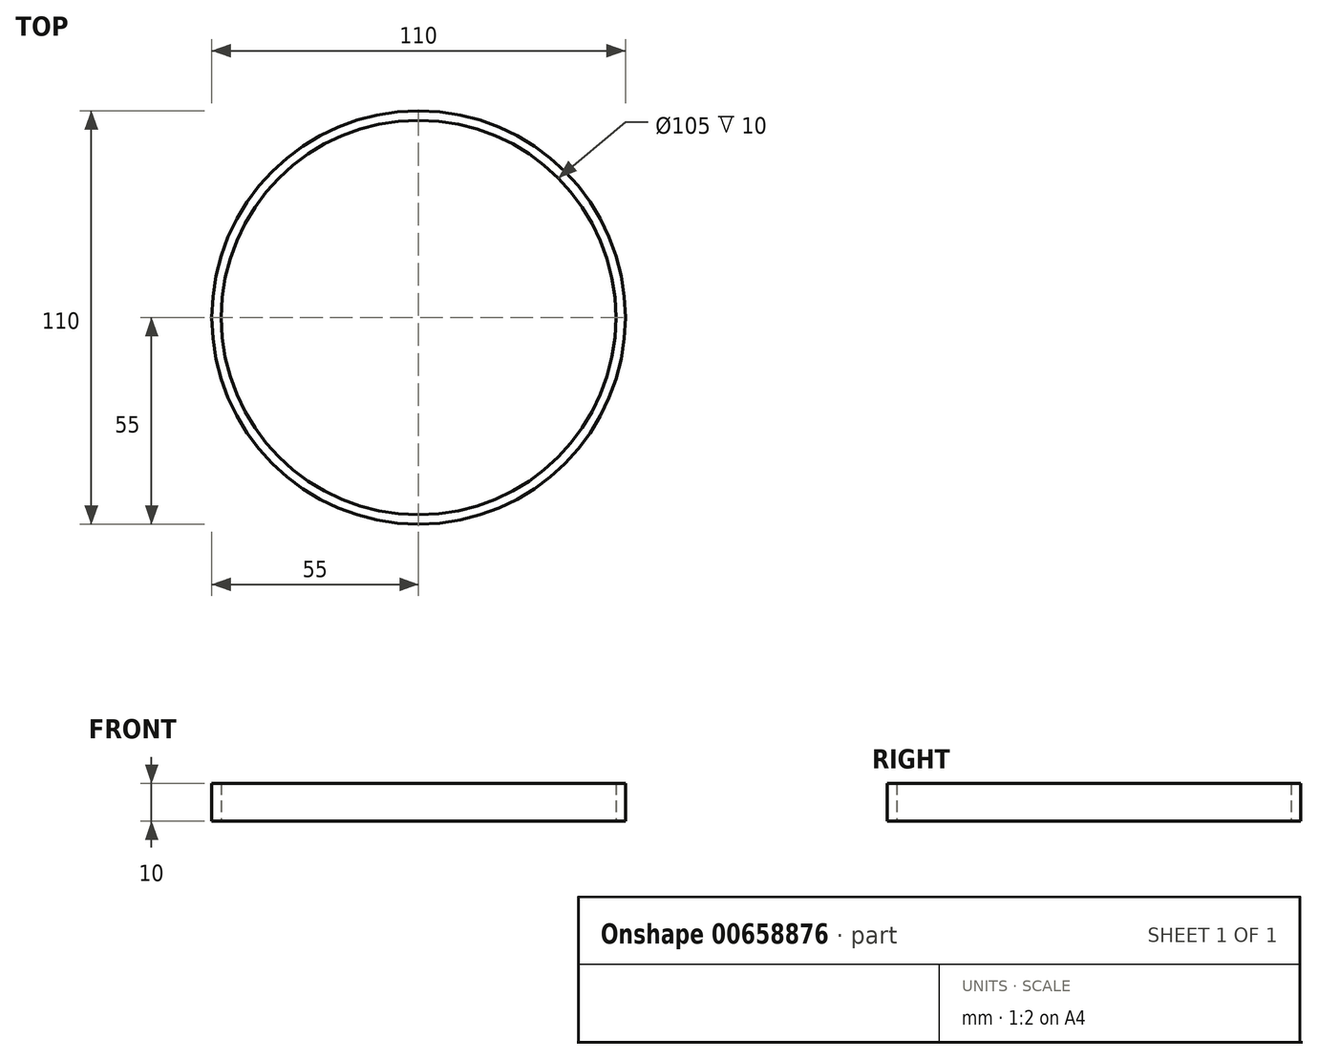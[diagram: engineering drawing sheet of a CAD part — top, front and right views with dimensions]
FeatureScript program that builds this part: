
annotation { "Feature Type Name" : "Feature", "Feature Type Description" : "" }
export const myFeature = defineFeature(function(context is Context, id is Id, definition is map)
    precondition{}
    {
        {
            var Q0;
            Q0=qCreatedBy(makeId("Top.planeOp"),FACE);
            var sketch = newSketch(context, id + "F0", { "sketchPlane" : qUnion([Q0])});
            skCircle(sketch, "E0", {"center": v(0, 0) * mm, "radius": 52.5 * mm});
            skCircle(sketch, "E1", {"center": v(0, 0) * mm, "radius": 55 * mm});
            skSolve(sketch);
        }
        {
            var Q0;
            Q0 = qSketchRegion(id + "F0", true);
            extrude(context, id + "F1", {"entities" : qUnion([Q0]), "depth" : 10 * mm, "offsetDistance" : 25 * mm});
        }
    });
